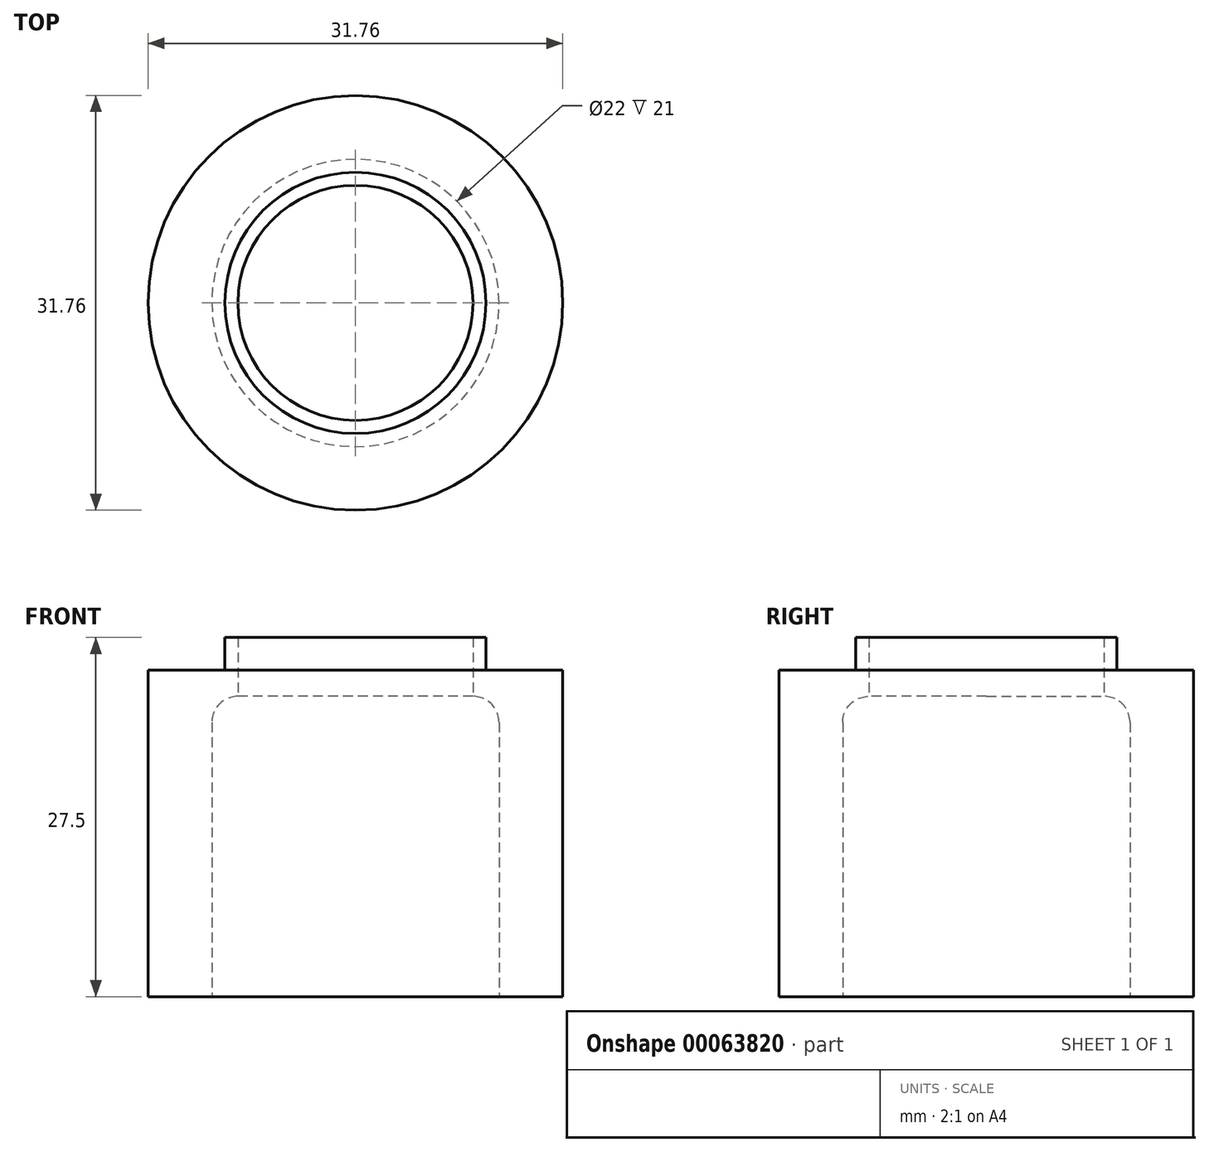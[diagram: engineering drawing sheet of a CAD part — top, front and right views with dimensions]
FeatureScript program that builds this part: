
annotation { "Feature Type Name" : "Feature", "Feature Type Description" : "" }
export const myFeature = defineFeature(function(context is Context, id is Id, definition is map)
    precondition{}
    {
        {
            var Q0;
            Q0=qCreatedBy(makeId("Top.planeOp"),FACE);
            var sketch = newSketch(context, id + "F0", { "sketchPlane" : qUnion([Q0])});
            skCircle(sketch, "E0", {"center": v(0, 0) * mm, "radius": 9 * mm});
            skCircle(sketch, "E1", {"center": v(0, 0) * mm, "radius": 15.88 * mm});
            skSolve(sketch);
        }
        {
            var Q0;
            Q0=makeQuery(id+"F0.imprint","IMPRINT",FACE,{"disambiguationData":[TD([[makeQuery(id+"F0.imprint","IMPRINT",EDGE,{"derivedFrom":sQuery(id+"F0.wireOp",EDGE,"E0")}),-1.0]])]});
            extrude(context, id + "F1", {"entities" : qUnion([Q0]), "depth" : 25 * mm});
        }
        {
            var Q0;
            Q0=makeQuery(id+"F1.opExtrude","CAP_FACE",FACE,{"disambiguationData":[OSD([sQuery(id+"F0.wireOp",EDGE,"E0"),sQuery(id+"F0.wireOp",EDGE,"E1")])],"isStart":false});
            var sketch = newSketch(context, id + "F2", { "sketchPlane" : qUnion([Q0])});
            skCircle(sketch, "E2", {"center": v(0, 0) * mm, "radius": 10 * mm});
            skSolve(sketch);
        }
        {
            var Q0;
            Q0=makeQuery(id+"F2.imprint","IMPRINT",FACE,{"disambiguationData":[TD([[makeQuery(id+"F2.imprint","IMPRINT",EDGE,{"derivedFrom":sQuery(id+"F2.wireOp",EDGE,"E2")}),1.0]])]});
            extrude(context, id + "F3", {"entities" : qUnion([Q0]), "operationType" : NewBodyOperationType.ADD, "depth" : 2.5 * mm});
        }
        {
            var Q0;
            Q0=makeQuery(id+"F1.opExtrude","CAP_FACE",FACE,{"disambiguationData":[OSD([sQuery(id+"F0.wireOp",EDGE,"E0"),sQuery(id+"F0.wireOp",EDGE,"E1")])],"isStart":true});
            var sketch = newSketch(context, id + "F4", { "sketchPlane" : qUnion([Q0])});
            skCircle(sketch, "E3", {"center": v(0, 0) * mm, "radius": 11 * mm});
            skSolve(sketch);
        }
        {
            var Q0;
            Q0=makeQuery(id+"F4.imprint","IMPRINT",FACE,{"disambiguationData":[TD([[makeQuery(id+"F4.imprint","IMPRINT",EDGE,{"derivedFrom":sQuery(id+"F4.wireOp",EDGE,"E3")}),1.0]])]});
            extrude(context, id + "F5", {"entities" : qUnion([Q0]), "operationType" : NewBodyOperationType.REMOVE, "oppositeDirection" : true, "depth" : 23 * mm});
        }
        {
            var Q0;
            Q0=makeQuery(id+"F5.boolean.opBoolean","COPY",EDGE,{"derivedFrom":makeQuery(id+"F5.opExtrude","CAP_EDGE",EDGE,{"disambiguationData":[OSD([sQuery(id+"F4.wireOp",EDGE,"E3")])],"isStart":false})});
            fillet(context, id + "F6", {"entities" : qUnion([Q0]), "radius" : 2 * mm, "tangentPropagation" : true, "allowEdgeOverflow" : false});
        }
        {
            var Q0;
            Q0=makeQuery(id+"F2.imprint","IMPRINT",FACE,{"disambiguationData":[TD([[makeQuery(id+"F2.imprint","IMPRINT",EDGE,{"derivedFrom":sQuery(id+"F2.wireOp",EDGE,"E2")}),1.0]])]});
            extrude(context, id + "F7", {"entities" : qUnion([Q0]), "operationType" : NewBodyOperationType.ADD, "depth" : 2.5 * mm});
        }
    });
